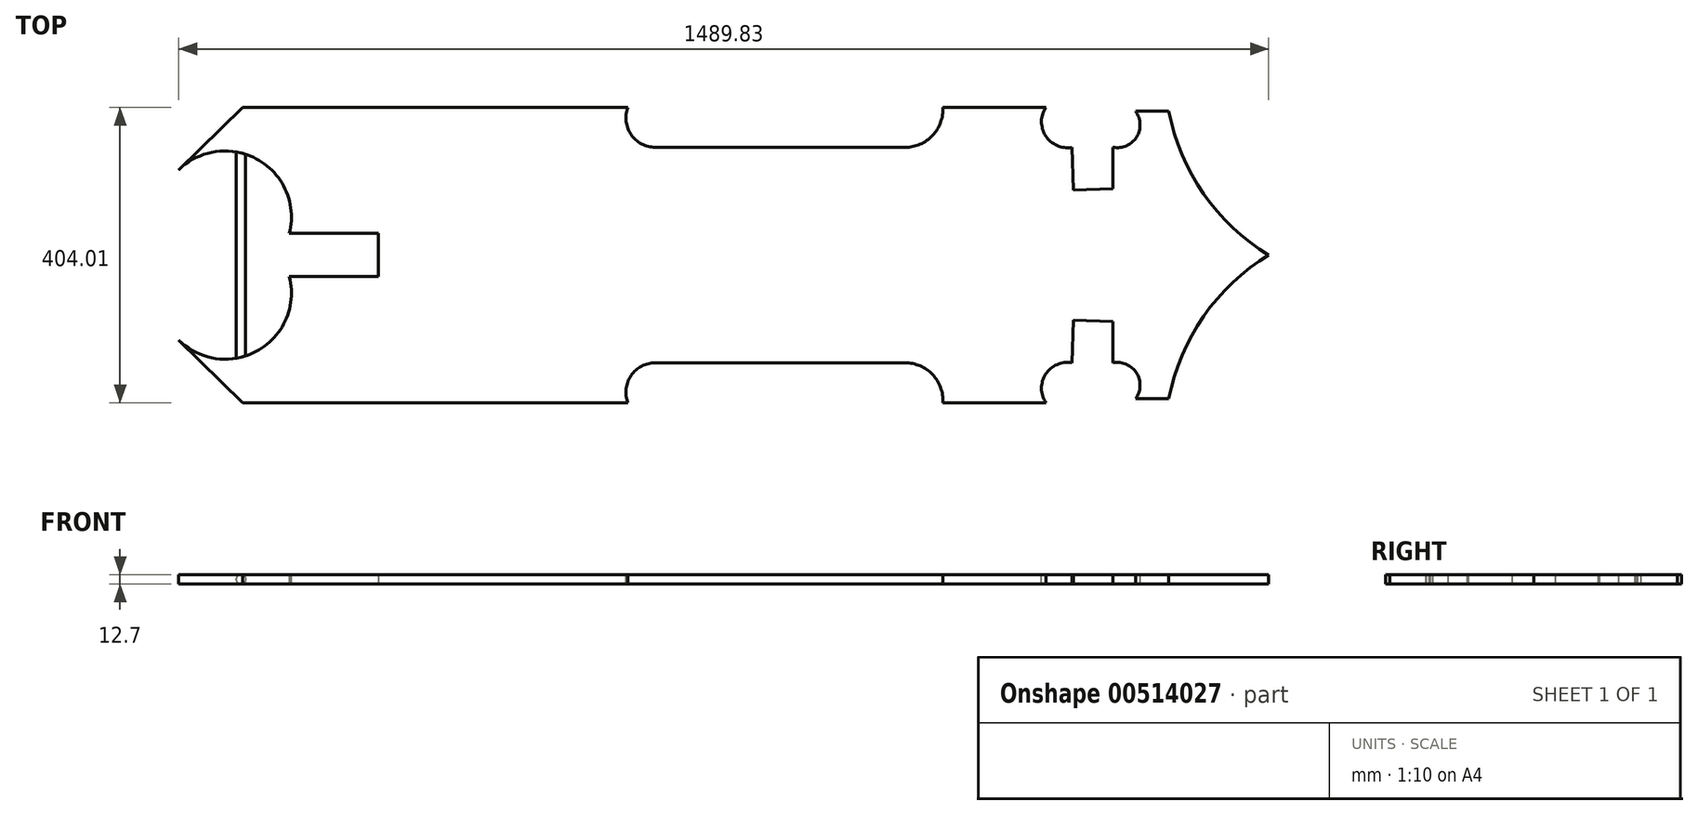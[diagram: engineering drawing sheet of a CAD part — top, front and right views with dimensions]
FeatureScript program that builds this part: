
annotation { "Feature Type Name" : "Feature", "Feature Type Description" : "" }
export const myFeature = defineFeature(function(context is Context, id is Id, definition is map)
    precondition{}
    {
        {
            var Q0;
            Q0=qCreatedBy(makeId("Front.planeOp"),FACE);
            var sketch = newSketch(context, id + "F0", { "sketchPlane" : qUnion([Q0])});
            skLineSegment(sketch, "E0", {"start": v(-555.4, 129.25) * mm, "end": v(-453.75, 229.45) * mm});
            skLineSegment(sketch, "E1", {"start": v(-453.75, 229.45) * mm, "end": v(54.25, 229.45) * mm});
            skLineSegment(sketch, "E2", {"start": v(92.66, 180.38) * mm, "end": v(422.12, 180.38) * mm});
            skLineSegment(sketch, "E3", {"start": v(469.64, 229.45) * mm, "end": v(640.2, 229.45) * mm});
            skLineSegment(sketch, "E4", {"start": v(664.06, 180.38) * mm, "end": v(664.06, 124.83) * mm});
            skLineSegment(sketch, "E5", {"start": v(664.06, 124.83) * mm, "end": v(715.54, 124.83) * mm});
            skLineSegment(sketch, "E6", {"start": v(715.54, 124.83) * mm, "end": v(715.54, 180.38) * mm});
            skLineSegment(sketch, "E7", {"start": v(736.13, 229.45) * mm, "end": v(785.04, 229.45) * mm});
            skPoint(sketch, "E8.end.orphan", {"position": v(54.25, -109.4) * mm});
            skLineSegment(sketch, "E9", {"start": v(55.25, -201.12) * mm, "end": v(-471.43, -201.12) * mm});
            skLineSegment(sketch, "E10", {"start": v(-471.43, -201.12) * mm, "end": v(-558.75, -115.53) * mm});
            skPoint(sketch, "E11.end.orphan", {"position": v(-420.32, 0) * mm});
            skPoint(sketch, "E12.end.orphan", {"position": v(92.66, -120.81) * mm});
            skPoint(sketch, "E12.start.orphan", {"position": v(422.12, -129.52) * mm});
            skPoint(sketch, "E13.end.orphan", {"position": v(469.64, -120.81) * mm});
            skLineSegment(sketch, "E14", {"start": v(92.66, -146.37) * mm, "end": v(433.91, -146.37) * mm});
            skLineSegment(sketch, "E15", {"start": v(485.66, -201.12) * mm, "end": v(626.48, -201.12) * mm});
            skPoint(sketch, "E16.end.orphan", {"position": v(640.2, -120.81) * mm});
            skPoint(sketch, "E17.end.orphan", {"position": v(664.06, -109.4) * mm});
            skPoint(sketch, "E18.end.orphan", {"position": v(664.06, -42.39) * mm});
            skPoint(sketch, "E19.end.orphan", {"position": v(715.54, -101.79) * mm});
            skPoint(sketch, "E20.end.orphan", {"position": v(736.13, -109.4) * mm});
            skLineSegment(sketch, "E21", {"start": v(662.07, -146.37) * mm, "end": v(664.06, -87.96) * mm});
            skLineSegment(sketch, "E22", {"start": v(664.06, -87.96) * mm, "end": v(718.4, -89.81) * mm});
            skLineSegment(sketch, "E23", {"start": v(718.4, -89.81) * mm, "end": v(718.4, -146.37) * mm});
            skLineSegment(sketch, "E24", {"start": v(749.17, -195.6) * mm, "end": v(794.52, -195.6) * mm});
            skPoint(sketch, "E25.orphan", {"position": v(785.04, -109.4) * mm});
            skArc(sketch, "E26", {"start": v(-420.32, 0) * mm, "mid": v(-423.23, 132.16) * mm, "end": v(-555.4, 129.25) * mm});
            skArc(sketch, "E27", {"start": v(-558.75, -115.53) * mm, "mid": v(-437.27, -120.39) * mm, "end": v(-420.32, 0) * mm});
            skArc(sketch, "E28", {"start": v(54.25, 229.45) * mm, "mid": v(61.5, 195.56) * mm, "end": v(92.66, 180.38) * mm});
            skArc(sketch, "E29", {"start": v(92.66, -146.37) * mm, "mid": v(59.5, -163.87) * mm, "end": v(55.25, -201.12) * mm});
            skArc(sketch, "E30", {"start": v(422.12, 180.38) * mm, "mid": v(456.27, 194.85) * mm, "end": v(469.64, 229.45) * mm});
            skArc(sketch, "E31", {"start": v(485.66, -201.12) * mm, "mid": v(471.58, -162.6) * mm, "end": v(433.91, -146.37) * mm});
            skArc(sketch, "E32", {"start": v(640.2, 229.45) * mm, "mid": v(638.41, 198.24) * mm, "end": v(664.06, 180.38) * mm});
            skArc(sketch, "E33", {"start": v(662.07, -146.37) * mm, "mid": v(626.2, -162) * mm, "end": v(626.48, -201.12) * mm});
            skArc(sketch, "E34", {"start": v(715.54, 180.38) * mm, "mid": v(741.08, 198.52) * mm, "end": v(736.13, 229.45) * mm});
            skArc(sketch, "E35", {"start": v(749.17, -195.6) * mm, "mid": v(750.5, -160.54) * mm, "end": v(718.4, -146.37) * mm});
            skPoint(sketch, "E36.end.orphan", {"position": v(923.09, -4.16) * mm});
            skPoint(sketch, "E37.start.orphan", {"position": v(923.09, 83.62) * mm});
            skArc(sketch, "E38", {"start": v(970.5, 20.98) * mm, "mid": v(855.33, -65.23) * mm, "end": v(794.52, -195.6) * mm});
            skLineSegment(sketch, "E39", {"start": v(970.5, 20.98) * mm, "end": v(1027.91, 45.04) * mm});
            skLineSegment(sketch, "E40", {"start": v(1027.91, 45.04) * mm, "end": v(970.34, 64.07) * mm});
            skArc(sketch, "E41", {"start": v(785.04, 229.45) * mm, "mid": v(860.04, 126.99) * mm, "end": v(970.34, 64.07) * mm});
            skSolve(sketch);
        }
        {
            var Q0;
            {var subQ0=sQuery(id+"F0.wireOp",EDGE,"E26");var subQ1=sQuery(id+"F0.wireOp",EDGE,"E0");var subQ2=makeQuery(id+"F0.imprint","INTERSECT",VERTEX,{"disambiguationData":[OD(0.0)],"derivedFrom":[subQ1,subQ0]});Q0=makeQuery(id+"F0.imprint","IMPRINT",FACE,{"disambiguationData":[TD([[makeQuery(id+"F0.imprint","IMPRINT",EDGE,{"disambiguationData":[TD([[subQ2,-1.0]])],"derivedFrom":subQ1}),1.0]])]});}
            var Q1;
            {var subQ4=sQuery(id+"F0.wireOp",EDGE,"E1");Q1=makeQuery(id+"F0.imprint","IMPRINT",FACE,{"disambiguationData":[TD([[makeQuery(id+"F0.imprint","IMPRINT",EDGE,{"derivedFrom":subQ4}),-1.0]])]});}
            extrude(context, id + "F1", {"entities" : qUnion([Q0, Q1]), "depth" : 12.7 * mm, "offsetDistance" : 25.4 * mm});
        }
        {
            var Q0;
            Q0=makeQuery(id+"F1.opExtrude","CAP_FACE",FACE,{"disambiguationData":[OSD([sQuery(id+"F0.wireOp",EDGE,"E0"),sQuery(id+"F0.wireOp",EDGE,"E1"),sQuery(id+"F0.wireOp",EDGE,"E2"),sQuery(id+"F0.wireOp",EDGE,"E3"),sQuery(id+"F0.wireOp",EDGE,"E4"),sQuery(id+"F0.wireOp",EDGE,"E5"),sQuery(id+"F0.wireOp",EDGE,"E6"),sQuery(id+"F0.wireOp",EDGE,"E7"),sQuery(id+"F0.wireOp",EDGE,"E9"),sQuery(id+"F0.wireOp",EDGE,"E10"),sQuery(id+"F0.wireOp",EDGE,"E14"),sQuery(id+"F0.wireOp",EDGE,"E15"),sQuery(id+"F0.wireOp",EDGE,"E21"),sQuery(id+"F0.wireOp",EDGE,"E22"),sQuery(id+"F0.wireOp",EDGE,"E23"),sQuery(id+"F0.wireOp",EDGE,"E24"),sQuery(id+"F0.wireOp",EDGE,"E26"),sQuery(id+"F0.wireOp",EDGE,"E27"),sQuery(id+"F0.wireOp",EDGE,"E28"),sQuery(id+"F0.wireOp",EDGE,"E29"),sQuery(id+"F0.wireOp",EDGE,"E30"),sQuery(id+"F0.wireOp",EDGE,"E31"),sQuery(id+"F0.wireOp",EDGE,"E32"),sQuery(id+"F0.wireOp",EDGE,"E33"),sQuery(id+"F0.wireOp",EDGE,"E34"),sQuery(id+"F0.wireOp",EDGE,"E35"),sQuery(id+"F0.wireOp",EDGE,"E38"),sQuery(id+"F0.wireOp",EDGE,"E39"),sQuery(id+"F0.wireOp",EDGE,"E40"),sQuery(id+"F0.wireOp",EDGE,"E41")])],"isStart":false});
            var sketch = newSketch(context, id + "F2", { "sketchPlane" : qUnion([Q0])});
            skLineSegment(sketch, "E42", {"start": v(-400.89, 30.36) * mm, "end": v(-285.72, 30.36) * mm});
            skPoint(sketch, "E43.end.orphan", {"position": v(-17.95, 0) * mm});
            skLineSegment(sketch, "E44", {"start": v(-285.72, 30.36) * mm, "end": v(-285.72, -28.6) * mm});
            skLineSegment(sketch, "E45", {"start": v(-285.72, -28.6) * mm, "end": v(-407.5, -28.6) * mm});
            skSolve(sketch);
        }
        {
            var Q0;
            {var subQ6=sQuery(id+"F2.wireOp",EDGE,"E42");Q0=makeQuery(id+"F2.imprint","IMPRINT",FACE,{"disambiguationData":[TD([[makeQuery(id+"F2.imprint","IMPRINT",EDGE,{"derivedFrom":subQ6}),-1.0]])]});}
            extrude(context, id + "F3", {"entities" : qUnion([Q0]), "operationType" : NewBodyOperationType.REMOVE, "oppositeDirection" : true, "depth" : 25.4 * mm, "offsetDistance" : 25.4 * mm});
        }
        {
            var Q0;
            Q0=makeQuery(id+"F1.opExtrude","SWEPT_BODY",BODY,{"disambiguationData":[OSD([sQuery(id+"F0.wireOp",EDGE,"E0"),sQuery(id+"F0.wireOp",EDGE,"E1"),sQuery(id+"F0.wireOp",EDGE,"E2"),sQuery(id+"F0.wireOp",EDGE,"E3"),sQuery(id+"F0.wireOp",EDGE,"E4"),sQuery(id+"F0.wireOp",EDGE,"E5"),sQuery(id+"F0.wireOp",EDGE,"E6"),sQuery(id+"F0.wireOp",EDGE,"E7"),sQuery(id+"F0.wireOp",EDGE,"E9"),sQuery(id+"F0.wireOp",EDGE,"E10"),sQuery(id+"F0.wireOp",EDGE,"E14"),sQuery(id+"F0.wireOp",EDGE,"E15"),sQuery(id+"F0.wireOp",EDGE,"E21"),sQuery(id+"F0.wireOp",EDGE,"E22"),sQuery(id+"F0.wireOp",EDGE,"E23"),sQuery(id+"F0.wireOp",EDGE,"E24"),sQuery(id+"F0.wireOp",EDGE,"E26"),sQuery(id+"F0.wireOp",EDGE,"E27"),sQuery(id+"F0.wireOp",EDGE,"E28"),sQuery(id+"F0.wireOp",EDGE,"E29"),sQuery(id+"F0.wireOp",EDGE,"E30"),sQuery(id+"F0.wireOp",EDGE,"E31"),sQuery(id+"F0.wireOp",EDGE,"E32"),sQuery(id+"F0.wireOp",EDGE,"E33"),sQuery(id+"F0.wireOp",EDGE,"E34"),sQuery(id+"F0.wireOp",EDGE,"E35"),sQuery(id+"F0.wireOp",EDGE,"E38"),sQuery(id+"F0.wireOp",EDGE,"E39"),sQuery(id+"F0.wireOp",EDGE,"E40"),sQuery(id+"F0.wireOp",EDGE,"E41")])]});
            var Q1;
            Q1=makeQuery(id+"F1.opExtrude","CAP_EDGE",EDGE,{"disambiguationData":[OSD([sQuery(id+"F0.wireOp",EDGE,"E9")])],"isStart":false});
            transform(context, id + "F4", {"entities" : qUnion([Q0]), "transformType" : TransformType.ROTATION, "transformAxis" : qUnion([Q1]), "angle" : 90 * degree, "oppositeDirection" : true, "makeCopy" : false});
        }
        {
            var Q0;
            Q0=makeQuery(id+"F1.opExtrude","CAP_FACE",FACE,{"disambiguationData":[OSD([sQuery(id+"F0.wireOp",EDGE,"E0"),sQuery(id+"F0.wireOp",EDGE,"E1"),sQuery(id+"F0.wireOp",EDGE,"E2"),sQuery(id+"F0.wireOp",EDGE,"E3"),sQuery(id+"F0.wireOp",EDGE,"E4"),sQuery(id+"F0.wireOp",EDGE,"E5"),sQuery(id+"F0.wireOp",EDGE,"E6"),sQuery(id+"F0.wireOp",EDGE,"E7"),sQuery(id+"F0.wireOp",EDGE,"E9"),sQuery(id+"F0.wireOp",EDGE,"E10"),sQuery(id+"F0.wireOp",EDGE,"E14"),sQuery(id+"F0.wireOp",EDGE,"E15"),sQuery(id+"F0.wireOp",EDGE,"E21"),sQuery(id+"F0.wireOp",EDGE,"E22"),sQuery(id+"F0.wireOp",EDGE,"E23"),sQuery(id+"F0.wireOp",EDGE,"E24"),sQuery(id+"F0.wireOp",EDGE,"E26"),sQuery(id+"F0.wireOp",EDGE,"E27"),sQuery(id+"F0.wireOp",EDGE,"E28"),sQuery(id+"F0.wireOp",EDGE,"E29"),sQuery(id+"F0.wireOp",EDGE,"E30"),sQuery(id+"F0.wireOp",EDGE,"E31"),sQuery(id+"F0.wireOp",EDGE,"E32"),sQuery(id+"F0.wireOp",EDGE,"E33"),sQuery(id+"F0.wireOp",EDGE,"E34"),sQuery(id+"F0.wireOp",EDGE,"E35"),sQuery(id+"F0.wireOp",EDGE,"E38"),sQuery(id+"F0.wireOp",EDGE,"E39"),sQuery(id+"F0.wireOp",EDGE,"E40"),sQuery(id+"F0.wireOp",EDGE,"E41")])],"isStart":true});
            var sketch = newSketch(context, id + "F5", { "sketchPlane" : qUnion([Q0])});
            skLineSegment(sketch, "E46", {"start": v(-479.9, -73.72) * mm, "end": v(-479.9, -371.58) * mm});
            skLineSegment(sketch, "E47", {"start": v(-479.9, -371.58) * mm, "end": v(-479.9, -222.65) * mm});
            skLineSegment(sketch, "E48", {"start": v(-467.2, -76.87) * mm, "end": v(-467.2, -369.61) * mm});
            skLineSegment(sketch, "E49", {"start": v(-479.9, -222.65) * mm, "end": v(-467.2, -222.65) * mm, "construction": true});
            skLineSegment(sketch, "E50", {"start": v(-479.9, -222.65) * mm, "end": v(-467.2, -222.65) * mm});
            skSolve(sketch);
        }
        {
            var Q0;
            {var subQ5=sQuery(id+"F5.wireOp",EDGE,"E46");Q0=makeQuery(id+"F5.imprint","IMPRINT",FACE,{"disambiguationData":[TD([[makeQuery(id+"F5.imprint","IMPRINT",EDGE,{"derivedFrom":subQ5}),1.0]])]});}
            extrude(context, id + "F6", {"entities" : qUnion([Q0]), "operationType" : NewBodyOperationType.ADD, "oppositeDirection" : true, "depth" : 12.7 * mm, "offsetDistance" : 25.4 * mm});
        }
        {
            var Q0;
            Q0=makeQuery(id+"F6.opExtrude","CAP_EDGE",EDGE,{"disambiguationData":[OSD([sQuery(id+"F5.wireOp",EDGE,"E48")])],"isStart":false});
            var Q1;
            Q1=makeQuery(id+"F6.opExtrude","CAP_EDGE",EDGE,{"disambiguationData":[OSD([sQuery(id+"F5.wireOp",EDGE,"E48")])],"isStart":true});
            var Q2;
            Q2=makeQuery(id+"F6.opExtrude","CAP_EDGE",EDGE,{"disambiguationData":[OSD([sQuery(id+"F5.wireOp",EDGE,"E46"),sQuery(id+"F5.wireOp",EDGE,"E47")])],"isStart":true});
            var Q3;
            Q3=makeQuery(id+"F6.opExtrude","CAP_EDGE",EDGE,{"disambiguationData":[OSD([sQuery(id+"F5.wireOp",EDGE,"E46"),sQuery(id+"F5.wireOp",EDGE,"E47")])],"isStart":false});
            fillet(context, id + "F7", {"entities" : qUnion([Q0, Q1, Q2, Q3]), "radius" : 6.35 * mm, "tangentPropagation" : true, "allowEdgeOverflow" : false});
        }
        {
            var Q0;
            {var subQ0=sQuery(id+"F0.wireOp",EDGE,"E27");var subQ1=sQuery(id+"F0.wireOp",EDGE,"E26");Q0=makeQuery(id+"F6.boolean.opBoolean","MERGE",FACE,{"derivedFrom":[makeQuery(id+"F1.opExtrude","CAP_FACE",FACE,{"disambiguationData":[OSD([sQuery(id+"F0.wireOp",EDGE,"E0"),sQuery(id+"F0.wireOp",EDGE,"E1"),sQuery(id+"F0.wireOp",EDGE,"E2"),sQuery(id+"F0.wireOp",EDGE,"E3"),sQuery(id+"F0.wireOp",EDGE,"E4"),sQuery(id+"F0.wireOp",EDGE,"E5"),sQuery(id+"F0.wireOp",EDGE,"E6"),sQuery(id+"F0.wireOp",EDGE,"E7"),sQuery(id+"F0.wireOp",EDGE,"E9"),sQuery(id+"F0.wireOp",EDGE,"E10"),sQuery(id+"F0.wireOp",EDGE,"E14"),sQuery(id+"F0.wireOp",EDGE,"E15"),sQuery(id+"F0.wireOp",EDGE,"E21"),sQuery(id+"F0.wireOp",EDGE,"E22"),sQuery(id+"F0.wireOp",EDGE,"E23"),sQuery(id+"F0.wireOp",EDGE,"E24"),subQ1,subQ0,sQuery(id+"F0.wireOp",EDGE,"E28"),sQuery(id+"F0.wireOp",EDGE,"E29"),sQuery(id+"F0.wireOp",EDGE,"E30"),sQuery(id+"F0.wireOp",EDGE,"E31"),sQuery(id+"F0.wireOp",EDGE,"E32"),sQuery(id+"F0.wireOp",EDGE,"E33"),sQuery(id+"F0.wireOp",EDGE,"E34"),sQuery(id+"F0.wireOp",EDGE,"E35"),sQuery(id+"F0.wireOp",EDGE,"E38"),sQuery(id+"F0.wireOp",EDGE,"E39"),sQuery(id+"F0.wireOp",EDGE,"E40"),sQuery(id+"F0.wireOp",EDGE,"E41")])],"isStart":true}),makeQuery(id+"F6.opExtrude","CAP_FACE",FACE,{"disambiguationData":[OSD([subQ1,subQ0,sQuery(id+"F5.wireOp",EDGE,"E46"),sQuery(id+"F5.wireOp",EDGE,"E47"),sQuery(id+"F5.wireOp",EDGE,"E48")])],"isStart":true})]});}
            var sketch = newSketch(context, id + "F8", { "sketchPlane" : qUnion([Q0])});
            skLineSegment(sketch, "E51", {"start": v(-481.64, -214.7) * mm, "end": v(931.08, -214.7) * mm});
            skPoint(sketch, "E51.startSnap0", {"position": v(-285.72, -214.7) * mm});
            skSolve(sketch);
        }
        {
            var Q0;
            {var subQ25=sQuery(id+"F0.wireOp",EDGE,"E1");Q0=makeQuery(id+"F8.imprint","IMPRINT",FACE,{"disambiguationData":[TD([[makeQuery(id+"F8.imprint","IMPRINT",EDGE,{"derivedFrom":makeQuery(id+"F1.opExtrude","CAP_EDGE",EDGE,{"disambiguationData":[OSD([subQ25])],"isStart":true})}),1.0]])]});}
            extrude(context, id + "F9", {"entities" : qUnion([Q0]), "operationType" : NewBodyOperationType.REMOVE, "oppositeDirection" : true, "depth" : 25.4 * mm, "offsetDistance" : 25.4 * mm});
        }
        {
            var Q0;
            Q0=makeQuery(id+"F1.opExtrude","SWEPT_BODY",BODY,{"disambiguationData":[OSD([sQuery(id+"F0.wireOp",EDGE,"E0"),sQuery(id+"F0.wireOp",EDGE,"E1"),sQuery(id+"F0.wireOp",EDGE,"E2"),sQuery(id+"F0.wireOp",EDGE,"E3"),sQuery(id+"F0.wireOp",EDGE,"E4"),sQuery(id+"F0.wireOp",EDGE,"E5"),sQuery(id+"F0.wireOp",EDGE,"E6"),sQuery(id+"F0.wireOp",EDGE,"E7"),sQuery(id+"F0.wireOp",EDGE,"E9"),sQuery(id+"F0.wireOp",EDGE,"E10"),sQuery(id+"F0.wireOp",EDGE,"E14"),sQuery(id+"F0.wireOp",EDGE,"E15"),sQuery(id+"F0.wireOp",EDGE,"E21"),sQuery(id+"F0.wireOp",EDGE,"E22"),sQuery(id+"F0.wireOp",EDGE,"E23"),sQuery(id+"F0.wireOp",EDGE,"E24"),sQuery(id+"F0.wireOp",EDGE,"E26"),sQuery(id+"F0.wireOp",EDGE,"E27"),sQuery(id+"F0.wireOp",EDGE,"E28"),sQuery(id+"F0.wireOp",EDGE,"E29"),sQuery(id+"F0.wireOp",EDGE,"E30"),sQuery(id+"F0.wireOp",EDGE,"E31"),sQuery(id+"F0.wireOp",EDGE,"E32"),sQuery(id+"F0.wireOp",EDGE,"E33"),sQuery(id+"F0.wireOp",EDGE,"E34"),sQuery(id+"F0.wireOp",EDGE,"E35"),sQuery(id+"F0.wireOp",EDGE,"E38"),sQuery(id+"F0.wireOp",EDGE,"E39"),sQuery(id+"F0.wireOp",EDGE,"E40"),sQuery(id+"F0.wireOp",EDGE,"E41")])]});
            var Q1;
            Q1=makeQuery(id+"F9.boolean.opBoolean","COPY",FACE,{"derivedFrom":makeQuery(id+"F9.opExtrude","SWEPT_FACE",FACE,{"disambiguationData":[OSD([sQuery(id+"F8.wireOp",EDGE,"E51")])]})});
            mirror(context, id + "F10", {"operationType" : NewBodyOperationType.ADD, "entities" : qUnion([Q0]), "mirrorPlane" : qUnion([Q1])});
        }
    });
